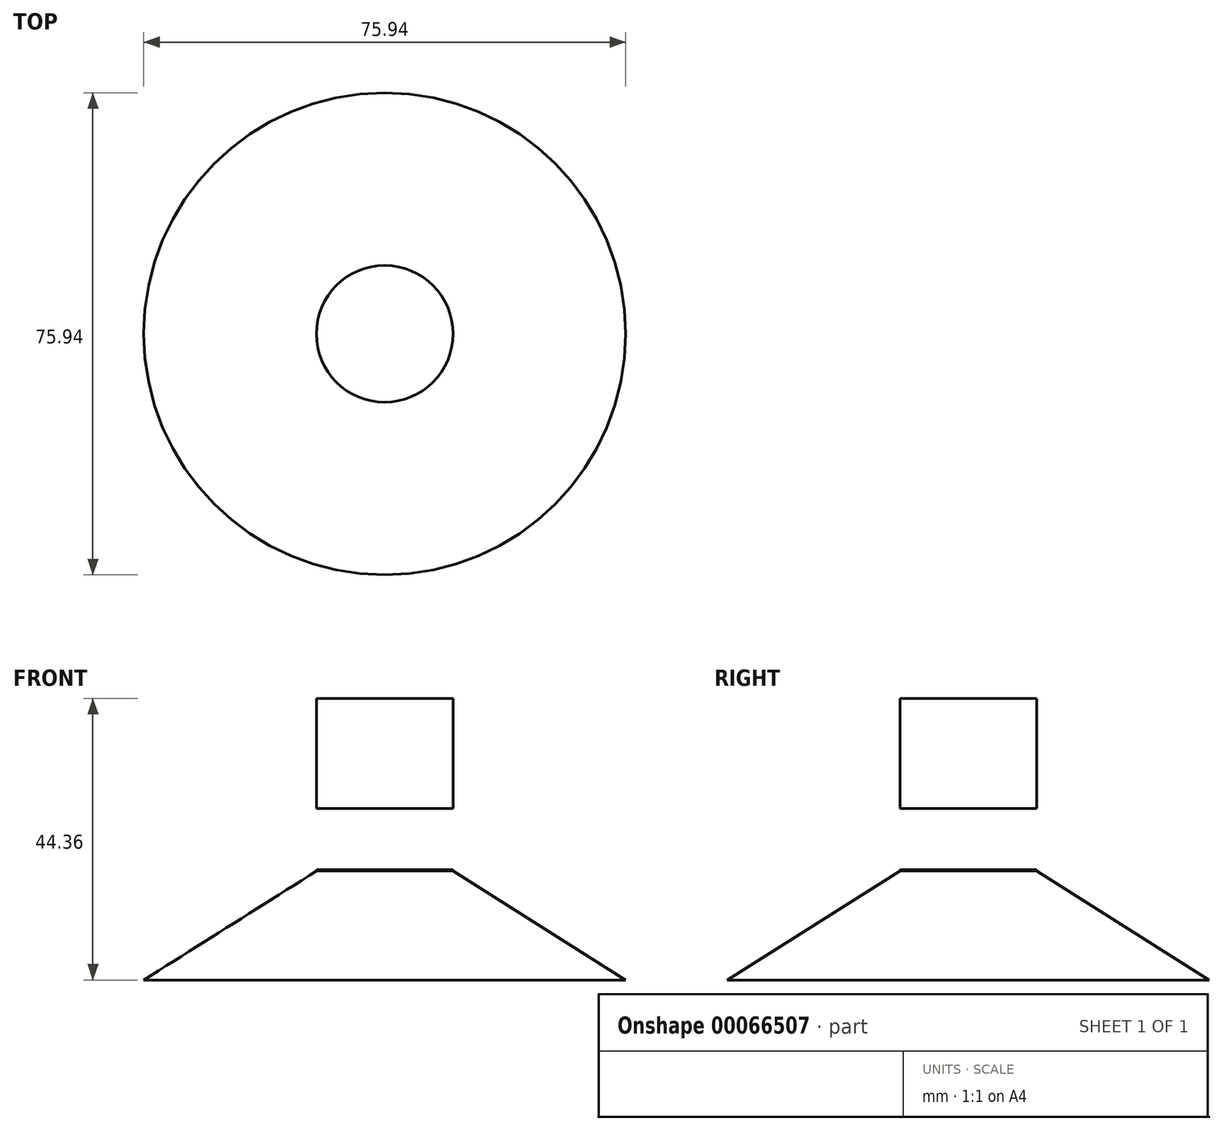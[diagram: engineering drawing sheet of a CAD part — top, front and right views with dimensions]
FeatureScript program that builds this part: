
annotation { "Feature Type Name" : "Feature", "Feature Type Description" : "" }
export const myFeature = defineFeature(function(context is Context, id is Id, definition is map)
    precondition{}
    {
        {
            var Q0;
            Q0=qCreatedBy(makeId("Front.planeOp"),FACE);
            var sketch = newSketch(context, id + "F0", { "sketchPlane" : qUnion([Q0])});
            skLineSegment(sketch, "E0", {"start": v(0, 0) * mm, "end": v(0, 44.36) * mm});
            skLineSegment(sketch, "E1", {"start": v(0, 44.36) * mm, "end": v(10.77, 44.36) * mm});
            skLineSegment(sketch, "E2", {"start": v(10.77, 44.36) * mm, "end": v(10.77, 17.16) * mm});
            skLineSegment(sketch, "E3", {"start": v(10.77, 17.16) * mm, "end": v(37.97, 0) * mm});
            skLineSegment(sketch, "E4", {"start": v(37.97, 0) * mm, "end": v(0, 0) * mm});
            skSolve(sketch);
        }
        {
            var Q0;
            Q0 = qSketchRegion(id + "F0", true);
            var Q1;
            Q1=sQuery(id+"F0.wireOp",EDGE,"E0");
            revolve(context, id + "F1", {"entities" : qUnion([Q0]), "axis" : qUnion([Q1]), "revolveType" : RevolveType.FULL});
        }
        {
            var Q0;
            Q0=qCreatedBy(makeId("Right.planeOp"),FACE);
            var sketch = newSketch(context, id + "F2", { "sketchPlane" : qUnion([Q0])});
            skLineSegment(sketch, "E5.bottom", {"start": v(-11.05, 27) * mm, "end": v(0, 27) * mm});
            skLineSegment(sketch, "E5.top", {"start": v(-11.05, 17.4) * mm, "end": v(0, 17.4) * mm});
            skLineSegment(sketch, "E5.left", {"start": v(-11.05, 27) * mm, "end": v(-11.05, 17.4) * mm});
            skLineSegment(sketch, "E5.right", {"start": v(0, 27) * mm, "end": v(0, 17.4) * mm});
            skSolve(sketch);
        }
        {
            var Q0;
            Q0 = qSketchRegion(id + "F2", true);
            var Q1;
            Q1=sQuery(id+"F2.wireOp",EDGE,"E5.right");
            revolve(context, id + "F3", {"operationType" : NewBodyOperationType.REMOVE, "entities" : qUnion([Q0]), "axis" : qUnion([Q1]), "revolveType" : RevolveType.FULL, "oppositeDirection" : true});
        }
    });
